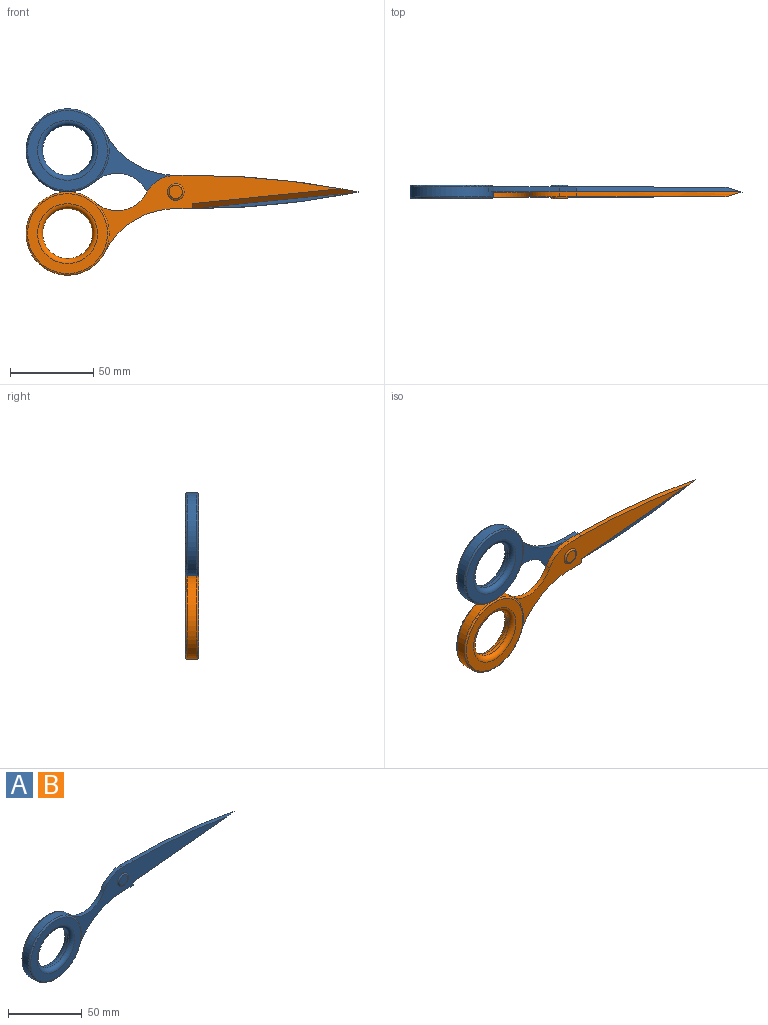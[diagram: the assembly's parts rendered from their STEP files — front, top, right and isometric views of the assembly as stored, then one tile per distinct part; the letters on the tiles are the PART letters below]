
ASSEMBLY  parts=2 mates=1
PART A: 20 faces, bbox 201.6x8x62.1 mm
  f0: plane 147.74x46.27mm, normal (0,-1,0), area 1612.7mm2, adj f2,f3,f4,f6,f7,f8,f13,f14
  f1: plane 157.99x46.27mm, normal (0,1,0), area 1974.5mm2, adj f2,f3,f4,f5,f6,f7,f8,f13
  f2: plane 10x3mm, normal (0,0,1), area 30mm2, adj f0,f1,f3,f8
  f3: cylinder r=20mm len=17.32mm, axis (0,1,0), area 62.8mm2, adj f0,f1,f2,f4
  f4: cylinder r=20mm len=31.17mm, axis (0,1,0), area 110.2mm2, adj f0,f1,f3,f5
  f5: cylinder r=25mm len=50mm, axis (0,1,0), area 843.7mm2, adj f1,f4,f6,f17,f18
  f6: cylinder r=47.81mm len=42.68mm, axis (0,1,0), area 158.3mm2, adj f0,f1,f5,f7
  f7: plane 10x3mm, normal (0,0,-1), area 30mm2, adj f0,f1,f6,f14
  f8: cylinder r=500mm len=99.5mm, axis (0,1,0), area 285mm2, adj f0,f1,f2,f13
  f9: plane 48x48mm, normal (0,1,0), area 791.7mm2, adj f15,f17
  f10: cylinder r=15mm len=30mm, axis (0,1,0), area 188.5mm2, adj f15,f16
  f11: plane 48x48mm, normal (0,-1,0), area 791.7mm2, adj f16,f18
  f12: plane 8x8mm, normal (0,-1,0), area 50.3mm2, adj f19
  f13: plane 99.5x11.97mm, normal (0.07,-0.71,-0.71), area 401.7mm2, adj f0,f1,f8,f14
  f14: plane 3x3mm, normal (1,0,0), area 4.5mm2, adj f0,f7,f13
  f15: torus R=18mm, axis (0,-1,0), area 476.4mm2, adj f9,f10
  f16: torus R=18mm, axis (0,-1,0), area 476.4mm2, adj f10,f11
  f17: torus R=24mm, axis (0,-1,0), area 243.2mm2, adj f5,f9
  f18: torus R=24mm, axis (0,-1,0), area 243.2mm2, adj f0,f5,f11
  f19: torus R=4mm, axis (0,-1,0), area 45.8mm2, adj f0,f12
PART B: same geometry as A
PLACE A rot(axis=(1,0,0),180deg) t=(0,0,0)mm
PLACE B at identity fixed
MATE revolute B.f19 <-> A.f19  axis (0,-1,0) through (0,0,0)mm
